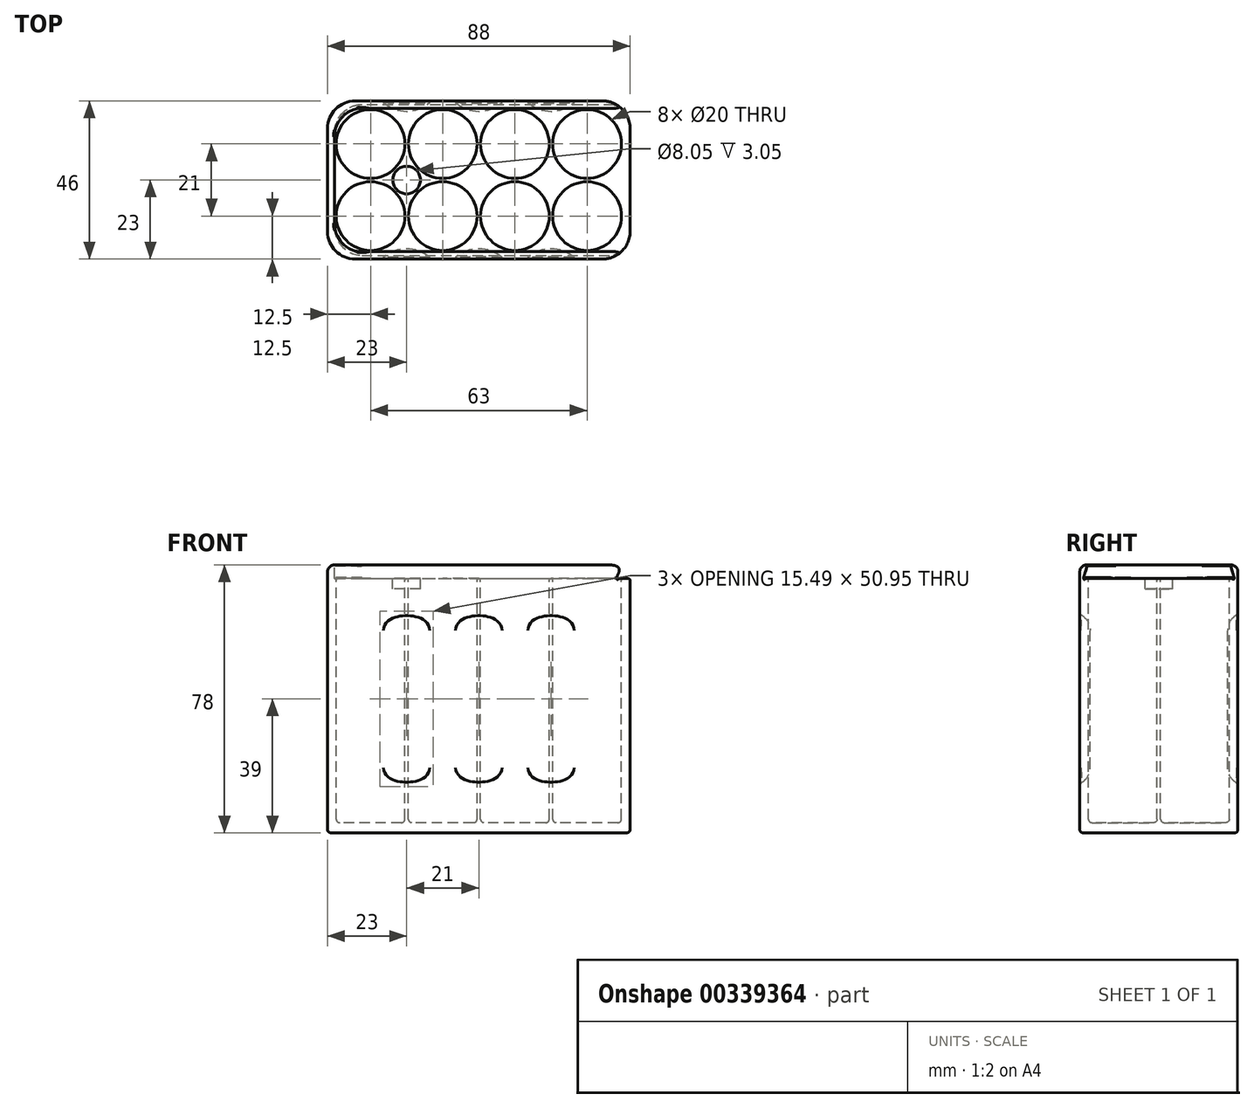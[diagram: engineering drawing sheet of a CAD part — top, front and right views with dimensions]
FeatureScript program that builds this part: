
annotation { "Feature Type Name" : "Feature", "Feature Type Description" : "" }
export const myFeature = defineFeature(function(context is Context, id is Id, definition is map)
    precondition{}
    {
        {
            var Q0;
            Q0=qCreatedBy(makeId("Top.planeOp"),FACE);
            var sketch = newSketch(context, id + "F0", { "sketchPlane" : qUnion([Q0])});
            skLineSegment(sketch, "E0.bottom", {"start": v(44, 23) * mm, "end": v(-44, 23) * mm});
            skLineSegment(sketch, "E0.top", {"start": v(44, -23) * mm, "end": v(-44, -23) * mm});
            skLineSegment(sketch, "E0.left", {"start": v(44, 23) * mm, "end": v(44, -23) * mm});
            skLineSegment(sketch, "E0.right", {"start": v(-44, 23) * mm, "end": v(-44, -23) * mm});
            skPoint(sketch, "E0.middle", {"position": v(0, 0) * mm});
            skSolve(sketch);
        }
        {
            var Q0;
            Q0 = qSketchRegion(id + "F0", true);
            extrude(context, id + "F1", {"entities" : qUnion([Q0]), "depth" : 78 * mm});
        }
        {
            var Q0;
            Q0=makeQuery(id+"F1.opExtrude","CAP_FACE",FACE,{"disambiguationData":[OSD([sQuery(id+"F0.wireOp",EDGE,"E0.bottom"),sQuery(id+"F0.wireOp",EDGE,"E0.top"),sQuery(id+"F0.wireOp",EDGE,"E0.left"),sQuery(id+"F0.wireOp",EDGE,"E0.right")])],"isStart":false});
            var sketch = newSketch(context, id + "F2", { "sketchPlane" : qUnion([Q0])});
            skCircle(sketch, "E1", {"center": v(-31.5, 10.5) * mm, "radius": 10 * mm});
            skCircle(sketch, "E2.0.1.0", {"center": v(-31.5, -10.5) * mm, "radius": 10 * mm});
            skCircle(sketch, "E2.1.0.0", {"center": v(-10.5, 10.5) * mm, "radius": 10 * mm});
            skCircle(sketch, "E2.1.1.0", {"center": v(-10.5, -10.5) * mm, "radius": 10 * mm});
            skCircle(sketch, "E2.2.0.0", {"center": v(10.5, 10.5) * mm, "radius": 10 * mm});
            skCircle(sketch, "E2.2.1.0", {"center": v(10.5, -10.5) * mm, "radius": 10 * mm});
            skCircle(sketch, "E2.3.0.0", {"center": v(31.5, 10.5) * mm, "radius": 10 * mm});
            skCircle(sketch, "E2.3.1.0", {"center": v(31.5, -10.5) * mm, "radius": 10 * mm});
            skLineSegment(sketch, "E2.direction1", {"start": v(-31.5, 10.5) * mm, "end": v(-10.5, 10.5) * mm, "construction": true});
            skLineSegment(sketch, "E2.direction2", {"start": v(-31.5, 10.5) * mm, "end": v(-31.5, -10.5) * mm, "construction": true});
            skSolve(sketch);
        }
        {
            var Q0;
            Q0 = qSketchRegion(id + "F2", true);
            extrude(context, id + "F3", {"entities" : qUnion([Q0]), "operationType" : NewBodyOperationType.REMOVE, "oppositeDirection" : true, "depth" : 75 * mm});
        }
        {
            var Q0;
            Q0=makeQuery(id+"F1.opExtrude","SWEPT_FACE",FACE,{"disambiguationData":[OSD([sQuery(id+"F0.wireOp",EDGE,"E0.left")])]});
            var sketch = newSketch(context, id + "F4", { "sketchPlane" : qUnion([Q0])});
            skLineSegment(sketch, "E3.bottom", {"start": v(-20.5, 78) * mm, "end": v(20.5, 78) * mm});
            skLineSegment(sketch, "E3.top", {"start": v(-20.5, 74) * mm, "end": v(20.5, 74) * mm});
            skLineSegment(sketch, "E3.left", {"start": v(-20.5, 78) * mm, "end": v(-20.5, 74) * mm});
            skLineSegment(sketch, "E3.right", {"start": v(20.5, 78) * mm, "end": v(20.5, 74) * mm});
            skPoint(sketch, "E4", {"position": v(-22, 74) * mm});
            skPoint(sketch, "E5", {"position": v(22, 74) * mm});
            skLineSegment(sketch, "E6", {"start": v(-20.5, 74) * mm, "end": v(-22, 74) * mm});
            skLineSegment(sketch, "E7", {"start": v(20.5, 78) * mm, "end": v(22, 74) * mm});
            skLineSegment(sketch, "E8", {"start": v(20.5, 74) * mm, "end": v(22, 74) * mm});
            skPoint(sketch, "E9", {"position": v(-20.5, 79) * mm});
            skLineSegment(sketch, "E10", {"start": v(-22, 74) * mm, "end": v(-20.5, 79) * mm});
            skLineSegment(sketch, "E11", {"start": v(-20.5, 79) * mm, "end": v(-20.5, 78) * mm});
            skPoint(sketch, "E12", {"position": v(20.5, 79) * mm});
            skLineSegment(sketch, "E13", {"start": v(22, 74) * mm, "end": v(20.5, 79) * mm});
            skLineSegment(sketch, "E14", {"start": v(20.5, 79) * mm, "end": v(20.5, 78) * mm});
            skLineSegment(sketch, "E15", {"start": v(20.5, 79) * mm, "end": v(-20.5, 79) * mm});
            skSolve(sketch);
        }
        {
            var Q0;
            Q0 = qSketchRegion(id + "F4", true);
            extrude(context, id + "F5", {"entities" : qUnion([Q0]), "operationType" : NewBodyOperationType.REMOVE, "oppositeDirection" : true, "depth" : 86 * mm});
        }
        {
            var Q0;
            Q0=makeQuery(id+"F1.opExtrude","SWEPT_EDGE",EDGE,{"disambiguationData":[OSD([sQuery(id+"F0.wireOp",EDGE,"E0.top"),sQuery(id+"F0.wireOp",EDGE,"E0.left")])]});
            var Q1;
            Q1=makeQuery(id+"F1.opExtrude","SWEPT_EDGE",EDGE,{"disambiguationData":[OSD([sQuery(id+"F0.wireOp",EDGE,"E0.bottom"),sQuery(id+"F0.wireOp",EDGE,"E0.left")])]});
            fillet(context, id + "F6", {"entities" : qUnion([Q0, Q1]), "radius" : 8 * mm, "tangentPropagation" : true, "allowEdgeOverflow" : false});
        }
        {
            var Q0;
            Q0=makeQuery(id+"F5.boolean.opBoolean","COPY",EDGE,{"derivedFrom":makeQuery(id+"F5.opExtrude","CAP_EDGE",EDGE,{"disambiguationData":[OSD([sQuery(id+"F4.wireOp",EDGE,"E10")])],"isStart":false})});
            var Q1;
            Q1=makeQuery(id+"F5.boolean.opBoolean","COPY",EDGE,{"derivedFrom":makeQuery(id+"F5.opExtrude","CAP_EDGE",EDGE,{"disambiguationData":[OSD([sQuery(id+"F4.wireOp",EDGE,"E13")])],"isStart":false})});
            fillet(context, id + "F7", {"entities" : qUnion([Q0, Q1]), "radius" : 8 * mm, "tangentPropagation" : true, "allowEdgeOverflow" : false});
        }
        {
            var Q0;
            Q0=makeQuery(id+"F1.opExtrude","SWEPT_EDGE",EDGE,{"disambiguationData":[OSD([sQuery(id+"F0.wireOp",EDGE,"E0.bottom"),sQuery(id+"F0.wireOp",EDGE,"E0.right")])]});
            var Q1;
            Q1=makeQuery(id+"F1.opExtrude","SWEPT_EDGE",EDGE,{"disambiguationData":[OSD([sQuery(id+"F0.wireOp",EDGE,"E0.top"),sQuery(id+"F0.wireOp",EDGE,"E0.right")])]});
            fillet(context, id + "F8", {"entities" : qUnion([Q0, Q1]), "radius" : 8 * mm, "tangentPropagation" : true, "allowEdgeOverflow" : false});
        }
        {
            var Q0;
            Q0=makeQuery(id+"F1.opExtrude","CAP_EDGE",EDGE,{"disambiguationData":[OSD([sQuery(id+"F0.wireOp",EDGE,"E0.top")])],"isStart":false});
            fillet(context, id + "F9", {"entities" : qUnion([Q0]), "radius" : 2 * mm, "tangentPropagation" : true, "allowEdgeOverflow" : false});
        }
        {
            var Q0;
            Q0=makeQuery(id+"F5.boolean.opBoolean","INTERSECT",EDGE,{"derivedFrom":[makeQuery(id+"F3.boolean.opBoolean","COPY",FACE,{"derivedFrom":makeQuery(id+"F3.opExtrude","SWEPT_FACE",FACE,{"disambiguationData":[OSD([sQuery(id+"F2.wireOp",EDGE,"E2.0.1.0")])]})}),makeQuery(id+"F5.opExtrude","SWEPT_FACE",FACE,{"disambiguationData":[OSD([sQuery(id+"F4.wireOp",EDGE,"E3.top"),sQuery(id+"F4.wireOp",EDGE,"E6"),sQuery(id+"F4.wireOp",EDGE,"E8")])]})]});
            var Q1;
            Q1=makeQuery(id+"F5.boolean.opBoolean","INTERSECT",EDGE,{"derivedFrom":[makeQuery(id+"F3.boolean.opBoolean","COPY",FACE,{"derivedFrom":makeQuery(id+"F3.opExtrude","SWEPT_FACE",FACE,{"disambiguationData":[OSD([sQuery(id+"F2.wireOp",EDGE,"E1")])]})}),makeQuery(id+"F5.opExtrude","SWEPT_FACE",FACE,{"disambiguationData":[OSD([sQuery(id+"F4.wireOp",EDGE,"E3.top"),sQuery(id+"F4.wireOp",EDGE,"E6"),sQuery(id+"F4.wireOp",EDGE,"E8")])]})]});
            var Q2;
            Q2=makeQuery(id+"F5.boolean.opBoolean","INTERSECT",EDGE,{"derivedFrom":[makeQuery(id+"F3.boolean.opBoolean","COPY",FACE,{"derivedFrom":makeQuery(id+"F3.opExtrude","SWEPT_FACE",FACE,{"disambiguationData":[OSD([sQuery(id+"F2.wireOp",EDGE,"E2.1.0.0")])]})}),makeQuery(id+"F5.opExtrude","SWEPT_FACE",FACE,{"disambiguationData":[OSD([sQuery(id+"F4.wireOp",EDGE,"E3.top"),sQuery(id+"F4.wireOp",EDGE,"E6"),sQuery(id+"F4.wireOp",EDGE,"E8")])]})]});
            var Q3;
            Q3=makeQuery(id+"F5.boolean.opBoolean","INTERSECT",EDGE,{"derivedFrom":[makeQuery(id+"F3.boolean.opBoolean","COPY",FACE,{"derivedFrom":makeQuery(id+"F3.opExtrude","SWEPT_FACE",FACE,{"disambiguationData":[OSD([sQuery(id+"F2.wireOp",EDGE,"E2.1.1.0")])]})}),makeQuery(id+"F5.opExtrude","SWEPT_FACE",FACE,{"disambiguationData":[OSD([sQuery(id+"F4.wireOp",EDGE,"E3.top"),sQuery(id+"F4.wireOp",EDGE,"E6"),sQuery(id+"F4.wireOp",EDGE,"E8")])]})]});
            var Q4;
            Q4=makeQuery(id+"F5.boolean.opBoolean","INTERSECT",EDGE,{"derivedFrom":[makeQuery(id+"F3.boolean.opBoolean","COPY",FACE,{"derivedFrom":makeQuery(id+"F3.opExtrude","SWEPT_FACE",FACE,{"disambiguationData":[OSD([sQuery(id+"F2.wireOp",EDGE,"E2.2.1.0")])]})}),makeQuery(id+"F5.opExtrude","SWEPT_FACE",FACE,{"disambiguationData":[OSD([sQuery(id+"F4.wireOp",EDGE,"E3.top"),sQuery(id+"F4.wireOp",EDGE,"E6"),sQuery(id+"F4.wireOp",EDGE,"E8")])]})]});
            var Q5;
            Q5=makeQuery(id+"F5.boolean.opBoolean","INTERSECT",EDGE,{"derivedFrom":[makeQuery(id+"F3.boolean.opBoolean","COPY",FACE,{"derivedFrom":makeQuery(id+"F3.opExtrude","SWEPT_FACE",FACE,{"disambiguationData":[OSD([sQuery(id+"F2.wireOp",EDGE,"E2.2.0.0")])]})}),makeQuery(id+"F5.opExtrude","SWEPT_FACE",FACE,{"disambiguationData":[OSD([sQuery(id+"F4.wireOp",EDGE,"E3.top"),sQuery(id+"F4.wireOp",EDGE,"E6"),sQuery(id+"F4.wireOp",EDGE,"E8")])]})]});
            var Q6;
            Q6=makeQuery(id+"F5.boolean.opBoolean","INTERSECT",EDGE,{"derivedFrom":[makeQuery(id+"F3.boolean.opBoolean","COPY",FACE,{"derivedFrom":makeQuery(id+"F3.opExtrude","SWEPT_FACE",FACE,{"disambiguationData":[OSD([sQuery(id+"F2.wireOp",EDGE,"E2.3.0.0")])]})}),makeQuery(id+"F5.opExtrude","SWEPT_FACE",FACE,{"disambiguationData":[OSD([sQuery(id+"F4.wireOp",EDGE,"E3.top"),sQuery(id+"F4.wireOp",EDGE,"E6"),sQuery(id+"F4.wireOp",EDGE,"E8")])]})]});
            var Q7;
            Q7=makeQuery(id+"F5.boolean.opBoolean","INTERSECT",EDGE,{"derivedFrom":[makeQuery(id+"F3.boolean.opBoolean","COPY",FACE,{"derivedFrom":makeQuery(id+"F3.opExtrude","SWEPT_FACE",FACE,{"disambiguationData":[OSD([sQuery(id+"F2.wireOp",EDGE,"E2.3.1.0")])]})}),makeQuery(id+"F5.opExtrude","SWEPT_FACE",FACE,{"disambiguationData":[OSD([sQuery(id+"F4.wireOp",EDGE,"E3.top"),sQuery(id+"F4.wireOp",EDGE,"E6"),sQuery(id+"F4.wireOp",EDGE,"E8")])]})]});
            fillet(context, id + "F10", {"entities" : qUnion([Q0, Q1, Q2, Q3, Q4, Q5, Q6, Q7]), "radius" : 0.5 * mm, "tangentPropagation" : true, "allowEdgeOverflow" : false});
        }
        {
            var Q0;
            Q0=makeQuery(id+"F6.opFillet","BLEND_EDGE",EDGE,{"blendedFrom":[makeQuery(id+"F1.opExtrude","SWEPT_EDGE",EDGE,{"disambiguationData":[OSD([sQuery(id+"F0.wireOp",EDGE,"E0.top"),sQuery(id+"F0.wireOp",EDGE,"E0.left")])]}),makeQuery(id+"F5.boolean.opBoolean","COPY",FACE,{"derivedFrom":makeQuery(id+"F5.opExtrude","SWEPT_FACE",FACE,{"disambiguationData":[OSD([sQuery(id+"F4.wireOp",EDGE,"E3.top"),sQuery(id+"F4.wireOp",EDGE,"E6"),sQuery(id+"F4.wireOp",EDGE,"E8")])]})})],"blendedInto":[makeQuery(id+"F5.boolean.opBoolean","COPY",FACE,{"derivedFrom":makeQuery(id+"F5.opExtrude","SWEPT_FACE",FACE,{"disambiguationData":[OSD([sQuery(id+"F4.wireOp",EDGE,"E3.top"),sQuery(id+"F4.wireOp",EDGE,"E6"),sQuery(id+"F4.wireOp",EDGE,"E8")])]})})]});
            fillet(context, id + "F11", {"entities" : qUnion([Q0]), "radius" : 0.5 * mm, "tangentPropagation" : true, "allowEdgeOverflow" : false});
        }
        {
            var Q0;
            Q0=makeQuery(id+"F9.opFillet","BLEND_EDGE",EDGE,{"blendedFrom":[makeQuery(id+"F1.opExtrude","CAP_EDGE",EDGE,{"disambiguationData":[OSD([sQuery(id+"F0.wireOp",EDGE,"E0.right")])],"isStart":false}),makeQuery(id+"F5.boolean.opBoolean","COPY",FACE,{"derivedFrom":makeQuery(id+"F5.opExtrude","CAP_FACE",FACE,{"disambiguationData":[OSD([sQuery(id+"F4.wireOp",EDGE,"E3.top"),sQuery(id+"F4.wireOp",EDGE,"E6"),sQuery(id+"F4.wireOp",EDGE,"E8"),sQuery(id+"F4.wireOp",EDGE,"E10"),sQuery(id+"F4.wireOp",EDGE,"E13"),sQuery(id+"F4.wireOp",EDGE,"E15")])],"isStart":false})})],"blendedInto":[makeQuery(id+"F5.boolean.opBoolean","COPY",FACE,{"derivedFrom":makeQuery(id+"F5.opExtrude","CAP_FACE",FACE,{"disambiguationData":[OSD([sQuery(id+"F4.wireOp",EDGE,"E3.top"),sQuery(id+"F4.wireOp",EDGE,"E6"),sQuery(id+"F4.wireOp",EDGE,"E8"),sQuery(id+"F4.wireOp",EDGE,"E10"),sQuery(id+"F4.wireOp",EDGE,"E13"),sQuery(id+"F4.wireOp",EDGE,"E15")])],"isStart":false})})]});
            fillet(context, id + "F12", {"entities" : qUnion([Q0]), "radius" : 0.25 * mm, "tangentPropagation" : true, "allowEdgeOverflow" : false});
        }
        {
            var Q0;
            {var subQ0=sQuery(id+"F0.wireOp",EDGE,"E0.left");var subQ1=sQuery(id+"F0.wireOp",EDGE,"E0.top");Q0=makeQuery(id+"F6.opFillet","BLEND_EDGE",EDGE,{"blendedFrom":[makeQuery(id+"F1.opExtrude","SWEPT_EDGE",EDGE,{"disambiguationData":[OSD([subQ1,subQ0])]}),makeQuery(id+"F1.opExtrude","CAP_FACE",FACE,{"disambiguationData":[OSD([sQuery(id+"F0.wireOp",EDGE,"E0.bottom"),subQ1,subQ0,sQuery(id+"F0.wireOp",EDGE,"E0.right")])],"isStart":true})],"blendedInto":[makeQuery(id+"F1.opExtrude","CAP_FACE",FACE,{"disambiguationData":[OSD([sQuery(id+"F0.wireOp",EDGE,"E0.bottom"),subQ1,subQ0,sQuery(id+"F0.wireOp",EDGE,"E0.right")])],"isStart":true})]});}
            var Q1;
            Q1=makeQuery(id+"F3.boolean.opBoolean","COPY",EDGE,{"derivedFrom":makeQuery(id+"F3.opExtrude","CAP_EDGE",EDGE,{"disambiguationData":[OSD([sQuery(id+"F2.wireOp",EDGE,"E2.0.1.0")])],"isStart":false})});
            var Q2;
            Q2=makeQuery(id+"F3.boolean.opBoolean","COPY",EDGE,{"derivedFrom":makeQuery(id+"F3.opExtrude","CAP_EDGE",EDGE,{"disambiguationData":[OSD([sQuery(id+"F2.wireOp",EDGE,"E2.1.1.0")])],"isStart":false})});
            var Q3;
            Q3=makeQuery(id+"F3.boolean.opBoolean","COPY",EDGE,{"derivedFrom":makeQuery(id+"F3.opExtrude","CAP_EDGE",EDGE,{"disambiguationData":[OSD([sQuery(id+"F2.wireOp",EDGE,"E2.1.0.0")])],"isStart":false})});
            var Q4;
            Q4=makeQuery(id+"F3.boolean.opBoolean","COPY",EDGE,{"derivedFrom":makeQuery(id+"F3.opExtrude","CAP_EDGE",EDGE,{"disambiguationData":[OSD([sQuery(id+"F2.wireOp",EDGE,"E1")])],"isStart":false})});
            var Q5;
            Q5=makeQuery(id+"F3.boolean.opBoolean","COPY",EDGE,{"derivedFrom":makeQuery(id+"F3.opExtrude","CAP_EDGE",EDGE,{"disambiguationData":[OSD([sQuery(id+"F2.wireOp",EDGE,"E2.2.1.0")])],"isStart":false})});
            var Q6;
            Q6=makeQuery(id+"F3.boolean.opBoolean","COPY",EDGE,{"derivedFrom":makeQuery(id+"F3.opExtrude","CAP_EDGE",EDGE,{"disambiguationData":[OSD([sQuery(id+"F2.wireOp",EDGE,"E2.2.0.0")])],"isStart":false})});
            var Q7;
            Q7=makeQuery(id+"F3.boolean.opBoolean","COPY",EDGE,{"derivedFrom":makeQuery(id+"F3.opExtrude","CAP_EDGE",EDGE,{"disambiguationData":[OSD([sQuery(id+"F2.wireOp",EDGE,"E2.3.1.0")])],"isStart":false})});
            var Q8;
            Q8=makeQuery(id+"F3.boolean.opBoolean","COPY",EDGE,{"derivedFrom":makeQuery(id+"F3.opExtrude","CAP_EDGE",EDGE,{"disambiguationData":[OSD([sQuery(id+"F2.wireOp",EDGE,"E2.3.0.0")])],"isStart":false})});
            fillet(context, id + "F13", {"entities" : qUnion([Q0, Q1, Q2, Q3, Q4, Q5, Q6, Q7, Q8]), "radius" : 1 * mm, "tangentPropagation" : true, "allowEdgeOverflow" : false});
        }
        {
            var Q0;
            Q0=qCreatedBy(makeId("Top.planeOp"),FACE);
            cPlane(context, id + "F14", {"entities" : qUnion([Q0]), "cplaneType" : CPlaneType.OFFSET, "offset" : 39 * mm, "width" : 150 * mm, "height" : 150 * mm});
        }
        {
            var Q0;
            Q0=qCreatedBy(id+"F14.planeOp",FACE);
            var sketch = newSketch(context, id + "F15", { "sketchPlane" : qUnion([Q0])});
            skPoint(sketch, "E16", {"position": v(0, -23) * mm});
            skCircle(sketch, "E17", {"center": v(0, -30) * mm, "radius": 10 * mm});
            skCircle(sketch, "E18.0.1.0", {"center": v(0, 30) * mm, "radius": 10 * mm});
            skCircle(sketch, "E18.1.0.0", {"center": v(21, -30) * mm, "radius": 10 * mm});
            skCircle(sketch, "E18.1.1.0", {"center": v(21, 30) * mm, "radius": 10 * mm});
            skLineSegment(sketch, "E18.direction1", {"start": v(0, -30) * mm, "end": v(21, -30) * mm, "construction": true});
            skLineSegment(sketch, "E18.direction2", {"start": v(0, -30) * mm, "end": v(0, 30) * mm, "construction": true});
            skCircle(sketch, "E19.1.0.0", {"center": v(-21, -30) * mm, "radius": 10 * mm});
            skCircle(sketch, "E19.1.1.0", {"center": v(-21, 30) * mm, "radius": 10 * mm});
            skLineSegment(sketch, "E19.direction1", {"start": v(0, -30) * mm, "end": v(-21, -30) * mm, "construction": true});
            skSolve(sketch);
        }
        {
            var Q0;
            Q0 = qSketchRegion(id + "F15", true);
            extrude(context, id + "F16", {"entities" : qUnion([Q0]), "operationType" : NewBodyOperationType.REMOVE, "oppositeDirection" : true, "depth" : 50 * mm, "symmetric" : true});
        }
        {
            var Q0;
            Q0=makeQuery(id+"F16.boolean.opBoolean","COPY",EDGE,{"derivedFrom":makeQuery(id+"F16.opExtrude","CAP_EDGE",EDGE,{"disambiguationData":[OSD([sQuery(id+"F15.wireOp",EDGE,"E19.1.0.0")])],"isStart":false})});
            var Q1;
            Q1=makeQuery(id+"F16.boolean.opBoolean","COPY",EDGE,{"derivedFrom":makeQuery(id+"F16.opExtrude","CAP_EDGE",EDGE,{"disambiguationData":[OSD([sQuery(id+"F15.wireOp",EDGE,"E17")])],"isStart":false})});
            var Q2;
            Q2=makeQuery(id+"F16.boolean.opBoolean","COPY",EDGE,{"derivedFrom":makeQuery(id+"F16.opExtrude","CAP_EDGE",EDGE,{"disambiguationData":[OSD([sQuery(id+"F15.wireOp",EDGE,"E18.1.0.0")])],"isStart":false})});
            var Q3;
            Q3=makeQuery(id+"F16.boolean.opBoolean","COPY",EDGE,{"derivedFrom":makeQuery(id+"F16.opExtrude","CAP_EDGE",EDGE,{"disambiguationData":[OSD([sQuery(id+"F15.wireOp",EDGE,"E18.1.0.0")])],"isStart":true})});
            var Q4;
            Q4=makeQuery(id+"F16.boolean.opBoolean","COPY",EDGE,{"derivedFrom":makeQuery(id+"F16.opExtrude","CAP_EDGE",EDGE,{"disambiguationData":[OSD([sQuery(id+"F15.wireOp",EDGE,"E17")])],"isStart":true})});
            var Q5;
            Q5=makeQuery(id+"F16.boolean.opBoolean","COPY",EDGE,{"derivedFrom":makeQuery(id+"F16.opExtrude","CAP_EDGE",EDGE,{"disambiguationData":[OSD([sQuery(id+"F15.wireOp",EDGE,"E19.1.0.0")])],"isStart":true})});
            var Q6;
            Q6=makeQuery(id+"F16.boolean.opBoolean","COPY",EDGE,{"derivedFrom":makeQuery(id+"F16.opExtrude","CAP_EDGE",EDGE,{"disambiguationData":[OSD([sQuery(id+"F15.wireOp",EDGE,"E19.1.1.0")])],"isStart":false})});
            var Q7;
            Q7=makeQuery(id+"F16.boolean.opBoolean","COPY",EDGE,{"derivedFrom":makeQuery(id+"F16.opExtrude","CAP_EDGE",EDGE,{"disambiguationData":[OSD([sQuery(id+"F15.wireOp",EDGE,"E18.0.1.0")])],"isStart":false})});
            var Q8;
            Q8=makeQuery(id+"F16.boolean.opBoolean","COPY",EDGE,{"derivedFrom":makeQuery(id+"F16.opExtrude","CAP_EDGE",EDGE,{"disambiguationData":[OSD([sQuery(id+"F15.wireOp",EDGE,"E18.1.1.0")])],"isStart":false})});
            var Q9;
            Q9=makeQuery(id+"F16.boolean.opBoolean","COPY",EDGE,{"derivedFrom":makeQuery(id+"F16.opExtrude","CAP_EDGE",EDGE,{"disambiguationData":[OSD([sQuery(id+"F15.wireOp",EDGE,"E19.1.1.0")])],"isStart":true})});
            var Q10;
            Q10=makeQuery(id+"F16.boolean.opBoolean","COPY",EDGE,{"derivedFrom":makeQuery(id+"F16.opExtrude","CAP_EDGE",EDGE,{"disambiguationData":[OSD([sQuery(id+"F15.wireOp",EDGE,"E18.0.1.0")])],"isStart":true})});
            var Q11;
            Q11=makeQuery(id+"F16.boolean.opBoolean","COPY",EDGE,{"derivedFrom":makeQuery(id+"F16.opExtrude","CAP_EDGE",EDGE,{"disambiguationData":[OSD([sQuery(id+"F15.wireOp",EDGE,"E18.1.1.0")])],"isStart":true})});
            fillet(context, id + "F17", {"entities" : qUnion([Q0, Q1, Q2, Q3, Q4, Q5, Q6, Q7, Q8, Q9, Q10, Q11]), "radius" : 5 * mm, "tangentPropagation" : true, "allowEdgeOverflow" : false});
        }
        {
            var Q0;
            Q0=makeQuery(id+"F16.boolean.opBoolean","INTERSECT",EDGE,{"disambiguationData":[OD(0.0)],"derivedFrom":[makeQuery(id+"F1.opExtrude","SWEPT_FACE",FACE,{"disambiguationData":[OSD([sQuery(id+"F0.wireOp",EDGE,"E0.bottom")])]}),makeQuery(id+"F16.opExtrude","SWEPT_FACE",FACE,{"disambiguationData":[OSD([sQuery(id+"F15.wireOp",EDGE,"E19.1.1.0")])]})]});
            var Q1;
            Q1=makeQuery(id+"F16.boolean.opBoolean","INTERSECT",EDGE,{"disambiguationData":[OD(0.0)],"derivedFrom":[makeQuery(id+"F1.opExtrude","SWEPT_FACE",FACE,{"disambiguationData":[OSD([sQuery(id+"F0.wireOp",EDGE,"E0.bottom")])]}),makeQuery(id+"F16.opExtrude","SWEPT_FACE",FACE,{"disambiguationData":[OSD([sQuery(id+"F15.wireOp",EDGE,"E18.0.1.0")])]})]});
            var Q2;
            Q2=makeQuery(id+"F16.boolean.opBoolean","INTERSECT",EDGE,{"disambiguationData":[OD(0.0)],"derivedFrom":[makeQuery(id+"F1.opExtrude","SWEPT_FACE",FACE,{"disambiguationData":[OSD([sQuery(id+"F0.wireOp",EDGE,"E0.bottom")])]}),makeQuery(id+"F16.opExtrude","SWEPT_FACE",FACE,{"disambiguationData":[OSD([sQuery(id+"F15.wireOp",EDGE,"E18.1.1.0")])]})]});
            var Q3;
            Q3=makeQuery(id+"F16.boolean.opBoolean","INTERSECT",EDGE,{"disambiguationData":[OD(1.0)],"derivedFrom":[makeQuery(id+"F1.opExtrude","SWEPT_FACE",FACE,{"disambiguationData":[OSD([sQuery(id+"F0.wireOp",EDGE,"E0.top")])]}),makeQuery(id+"F16.opExtrude","SWEPT_FACE",FACE,{"disambiguationData":[OSD([sQuery(id+"F15.wireOp",EDGE,"E18.1.0.0")])]})]});
            var Q4;
            Q4=makeQuery(id+"F16.boolean.opBoolean","INTERSECT",EDGE,{"disambiguationData":[OD(1.0)],"derivedFrom":[makeQuery(id+"F1.opExtrude","SWEPT_FACE",FACE,{"disambiguationData":[OSD([sQuery(id+"F0.wireOp",EDGE,"E0.top")])]}),makeQuery(id+"F16.opExtrude","SWEPT_FACE",FACE,{"disambiguationData":[OSD([sQuery(id+"F15.wireOp",EDGE,"E17")])]})]});
            var Q5;
            Q5=makeQuery(id+"F16.boolean.opBoolean","INTERSECT",EDGE,{"disambiguationData":[OD(0.0)],"derivedFrom":[makeQuery(id+"F1.opExtrude","SWEPT_FACE",FACE,{"disambiguationData":[OSD([sQuery(id+"F0.wireOp",EDGE,"E0.top")])]}),makeQuery(id+"F16.opExtrude","SWEPT_FACE",FACE,{"disambiguationData":[OSD([sQuery(id+"F15.wireOp",EDGE,"E19.1.0.0")])]})]});
            fillet(context, id + "F18", {"entities" : qUnion([Q0, Q1, Q2, Q3, Q4, Q5]), "radius" : 1.5 * mm, "tangentPropagation" : true, "allowEdgeOverflow" : false});
        }
        {
            var Q0;
            Q0=makeQuery(id+"F10.opFillet","SPLIT",FACE,{"disambiguationData":[OD(2.0)],"derivedFrom":makeQuery(id+"F5.boolean.opBoolean","COPY",FACE,{"derivedFrom":makeQuery(id+"F5.opExtrude","SWEPT_FACE",FACE,{"disambiguationData":[OSD([sQuery(id+"F4.wireOp",EDGE,"E3.top"),sQuery(id+"F4.wireOp",EDGE,"E6"),sQuery(id+"F4.wireOp",EDGE,"E8")])]})})});
            var sketch = newSketch(context, id + "F19", { "sketchPlane" : qUnion([Q0])});
            skPoint(sketch, "E20", {"position": v(-21, 0) * mm});
            skCircle(sketch, "E21", {"center": v(-21, 0) * mm, "radius": 4.03 * mm});
            skSolve(sketch);
        }
        {
            var Q0;
            Q0 = qSketchRegion(id + "F19", true);
            extrude(context, id + "F20", {"entities" : qUnion([Q0]), "operationType" : NewBodyOperationType.REMOVE, "oppositeDirection" : true, "depth" : 3.05 * mm});
        }
        {
            var Q0;
            Q0=makeQuery(id+"F5.boolean.opBoolean","COPY",EDGE,{"derivedFrom":makeQuery(id+"F5.opExtrude","SWEPT_EDGE",EDGE,{"disambiguationData":[OSD([sQuery(id+"F4.wireOp",EDGE,"E6"),sQuery(id+"F4.wireOp",EDGE,"E10")])]})});
            fillet(context, id + "F21", {"entities" : qUnion([Q0]), "radius" : 0.25 * mm, "tangentPropagation" : true, "allowEdgeOverflow" : false});
        }
    });
